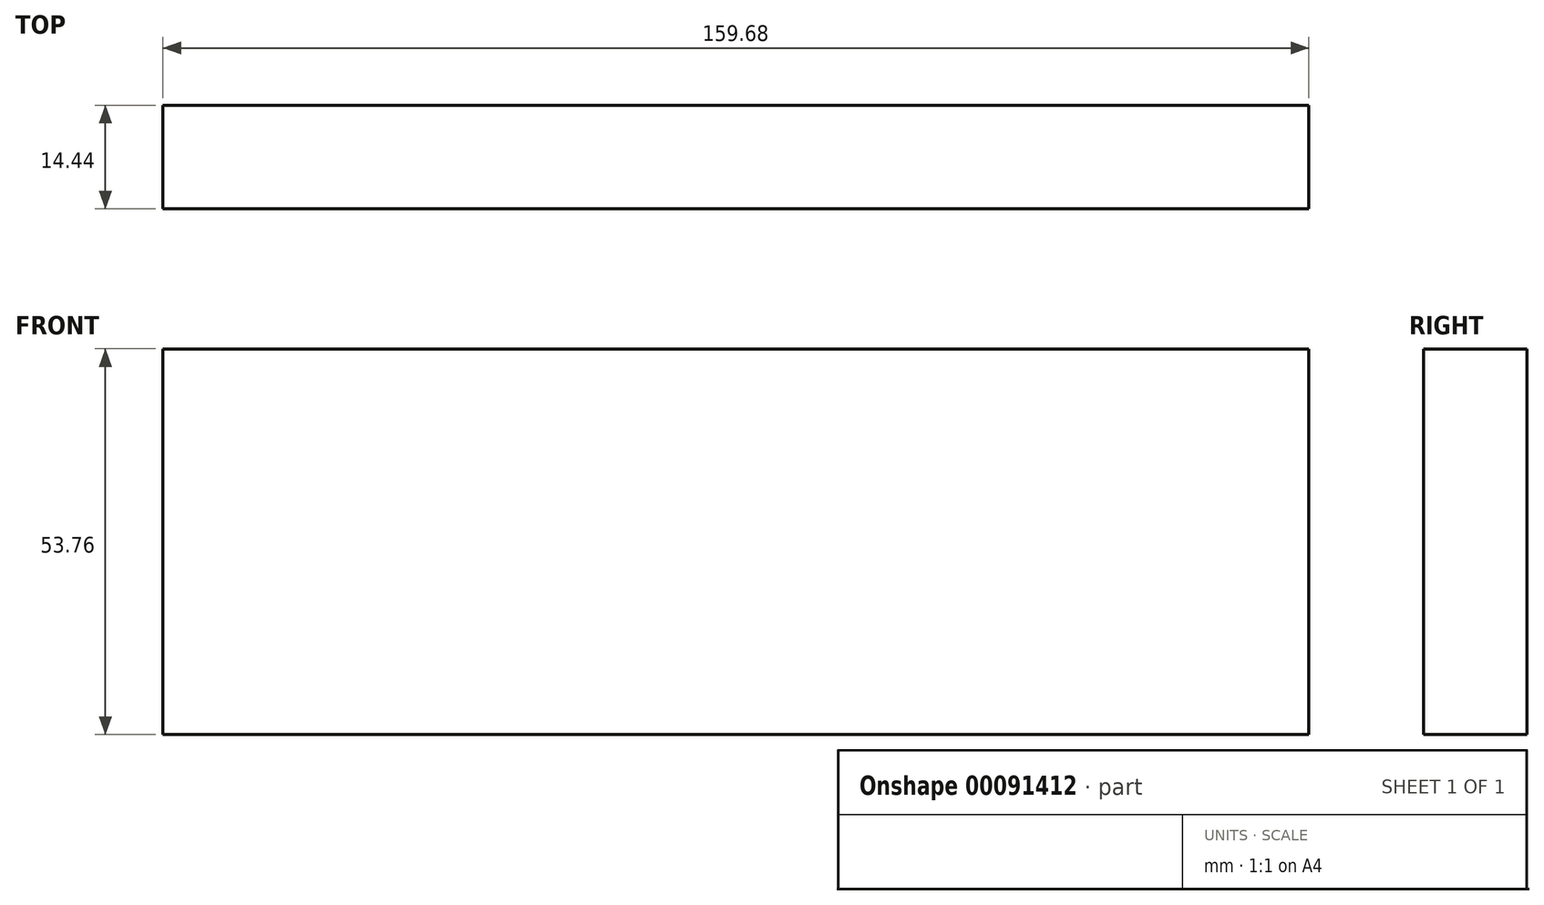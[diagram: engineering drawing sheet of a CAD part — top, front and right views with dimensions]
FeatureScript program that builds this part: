
annotation { "Feature Type Name" : "Feature", "Feature Type Description" : "" }
export const myFeature = defineFeature(function(context is Context, id is Id, definition is map)
    precondition{}
    {
        {
            var Q0;
            Q0=qCreatedBy(makeId("Front.planeOp"),FACE);
            var sketch = newSketch(context, id + "F0", { "sketchPlane" : qUnion([Q0])});
            skLineSegment(sketch, "E0.bottom", {"start": v(79.84, -26.88) * mm, "end": v(-79.84, -26.88) * mm});
            skLineSegment(sketch, "E0.top", {"start": v(79.84, 26.88) * mm, "end": v(-79.84, 26.88) * mm});
            skLineSegment(sketch, "E0.left", {"start": v(79.84, -26.88) * mm, "end": v(79.84, 26.88) * mm});
            skLineSegment(sketch, "E0.right", {"start": v(-79.84, -26.88) * mm, "end": v(-79.84, 26.88) * mm});
            skPoint(sketch, "E0.middle", {"position": v(0, 0) * mm});
            skSolve(sketch);
        }
        {
            var Q0;
            Q0=makeQuery(id+"F0.imprint","IMPRINT",FACE,{"disambiguationData":[TD([[makeQuery(id+"F0.imprint","IMPRINT",EDGE,{"derivedFrom":sQuery(id+"F0.wireOp",EDGE,"E0.bottom")}),-1.0]])]});
            extrude(context, id + "F1", {"entities" : qUnion([Q0]), "depth" : 14.44 * mm});
        }
    });
